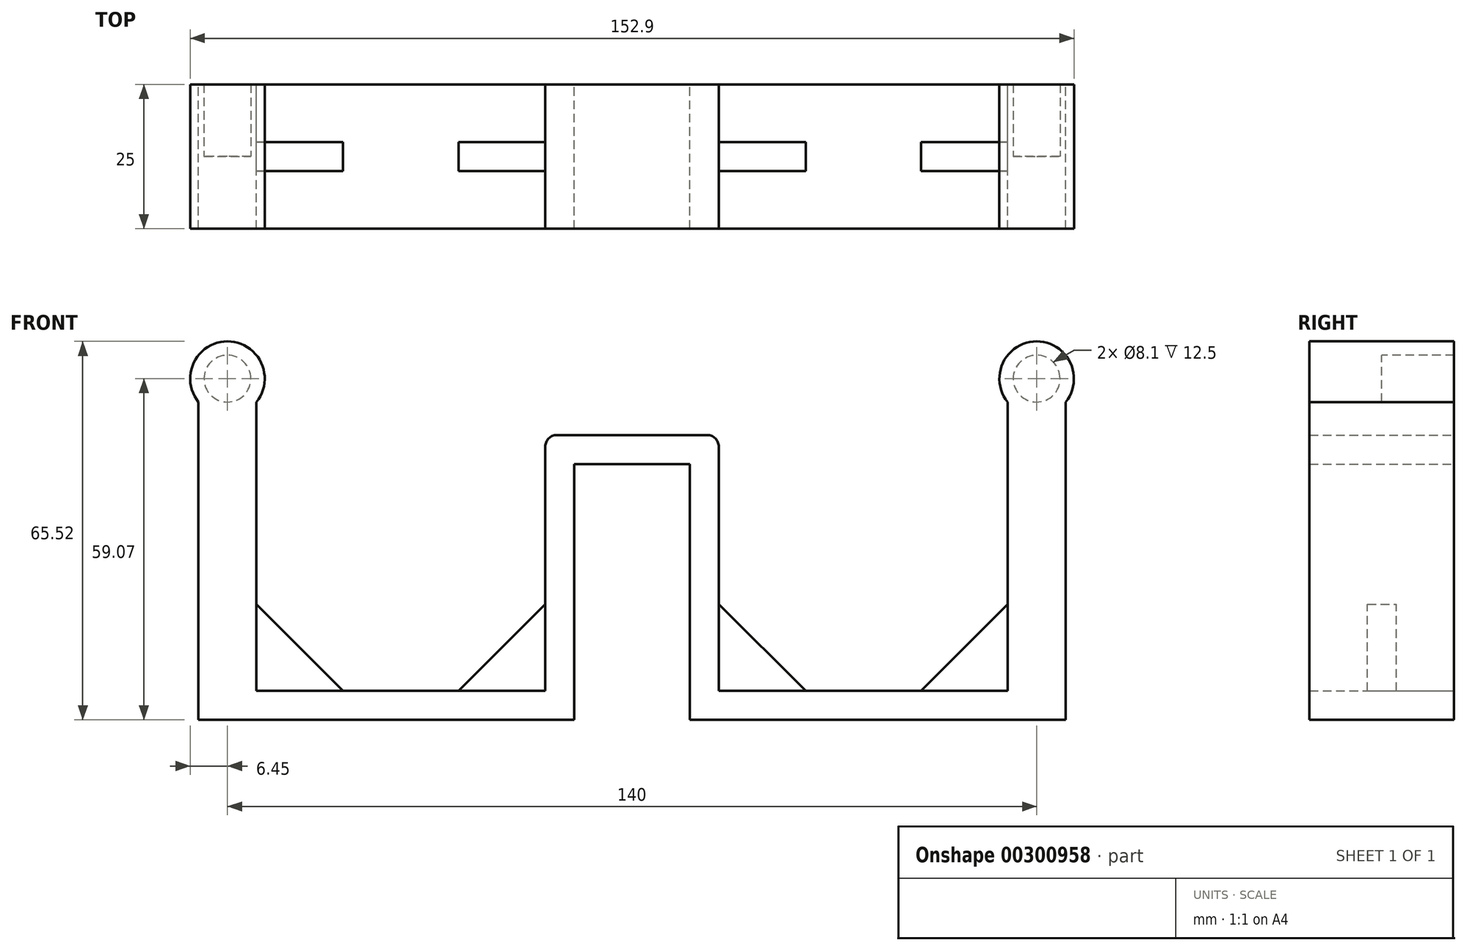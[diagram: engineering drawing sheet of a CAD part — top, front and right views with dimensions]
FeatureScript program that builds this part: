
annotation { "Feature Type Name" : "Feature", "Feature Type Description" : "" }
export const myFeature = defineFeature(function(context is Context, id is Id, definition is map)
    precondition{}
    {
        {
            var Q0;
            Q0=qCreatedBy(makeId("Front.planeOp"),FACE);
            var sketch = newSketch(context, id + "F0", { "sketchPlane" : qUnion([Q0])});
            skLineSegment(sketch, "E0", {"start": v(15, 0) * mm, "end": v(65, 0) * mm});
            skLineSegment(sketch, "E1", {"start": v(65, 0) * mm, "end": v(65, 50) * mm});
            skLineSegment(sketch, "E2", {"start": v(65, 50) * mm, "end": v(75, 50) * mm});
            skLineSegment(sketch, "E3", {"start": v(75, 50) * mm, "end": v(75, -5) * mm});
            skLineSegment(sketch, "E4", {"start": v(75, -5) * mm, "end": v(10, -5) * mm});
            skPoint(sketch, "E5", {"position": v(70, 50) * mm});
            skCircle(sketch, "E6", {"center": v(70, 54.07) * mm, "radius": 6.45 * mm});
            skPoint(sketch, "E7.start.orphan", {"position": v(10, 40) * mm});
            skLineSegment(sketch, "E8", {"start": v(15, 0) * mm, "end": v(15, 44.3) * mm});
            skLineSegment(sketch, "E9", {"start": v(15, 44.3) * mm, "end": v(0, 44.3) * mm});
            skLineSegment(sketch, "E10", {"start": v(0, 44.3) * mm, "end": v(0, 39.3) * mm});
            skLineSegment(sketch, "E11", {"start": v(0, 39.3) * mm, "end": v(10, 39.3) * mm});
            skLineSegment(sketch, "E12", {"start": v(10, 39.3) * mm, "end": v(10, -5) * mm});
            skSolve(sketch);
        }
        {
            var Q0;
            Q0=makeQuery(id+"F0.imprint","IMPRINT",FACE,{"disambiguationData":[TD([[makeQuery(id+"F0.imprint","IMPRINT",EDGE,{"derivedFrom":sQuery(id+"F0.wireOp",EDGE,"E0")}),-1.0]])]});
            var Q1;
            {var subQ0=sQuery(id+"F0.wireOp",EDGE,"E2");Q1=makeQuery(id+"F0.imprint","IMPRINT",FACE,{"disambiguationData":[TD([[makeQuery(id+"F0.imprint","IMPRINT",EDGE,{"derivedFrom":subQ0}),-1.0]])]});}
            var Q2;
            {var subQ0=sQuery(id+"F0.wireOp",EDGE,"E2");Q2=makeQuery(id+"F0.imprint","IMPRINT",FACE,{"disambiguationData":[TD([[makeQuery(id+"F0.imprint","IMPRINT",EDGE,{"derivedFrom":subQ0}),1.0]])]});}
            extrude(context, id + "F1", {"entities" : qUnion([Q0, Q1, Q2]), "endBound" : BoundingType.SYMMETRIC, "depth" : 25 * mm});
        }
        {
            var Q0;
            Q0=qCreatedBy(makeId("Front.planeOp"),FACE);
            var sketch = newSketch(context, id + "F2", { "sketchPlane" : qUnion([Q0])});
            skLineSegment(sketch, "E13", {"start": v(15.04, 0) * mm, "end": v(15.04, 15) * mm});
            skLineSegment(sketch, "E14", {"start": v(15.04, 15) * mm, "end": v(30.04, 0) * mm});
            skLineSegment(sketch, "E15", {"start": v(15.04, 0) * mm, "end": v(30.04, 0) * mm});
            skLineSegment(sketch, "E16", {"start": v(65, 0) * mm, "end": v(65, 15) * mm});
            skLineSegment(sketch, "E17", {"start": v(65, 15) * mm, "end": v(50, 0) * mm});
            skLineSegment(sketch, "E18", {"start": v(50, 0) * mm, "end": v(65, 0) * mm});
            skSolve(sketch);
        }
        {
            var Q0;
            Q0=makeQuery(id+"F2.imprint","IMPRINT",FACE,{"disambiguationData":[TD([[makeQuery(id+"F2.imprint","IMPRINT",EDGE,{"derivedFrom":sQuery(id+"F2.wireOp",EDGE,"E13")}),-1.0]])]});
            var Q1;
            Q1=makeQuery(id+"F2.imprint","IMPRINT",FACE,{"disambiguationData":[TD([[makeQuery(id+"F2.imprint","IMPRINT",EDGE,{"derivedFrom":sQuery(id+"F2.wireOp",EDGE,"E16")}),1.0]])]});
            extrude(context, id + "F3", {"entities" : qUnion([Q0, Q1]), "operationType" : NewBodyOperationType.ADD, "endBound" : BoundingType.SYMMETRIC, "depth" : 5 * mm});
        }
        {
            var Q0;
            Q0=makeQuery(id+"F1.opExtrude","SWEPT_EDGE",EDGE,{"disambiguationData":[OSD([sQuery(id+"F0.wireOp",EDGE,"E8"),sQuery(id+"F0.wireOp",EDGE,"E9")])]});
            var Q1;
            Q1=makeQuery(id+"F7.opPattern","COPY",EDGE,{"derivedFrom":makeQuery(id+"F1.opExtrude","SWEPT_EDGE",EDGE,{"disambiguationData":[OSD([sQuery(id+"F0.wireOp",EDGE,"E8"),sQuery(id+"F0.wireOp",EDGE,"E9")])]}),"instanceName":"1"});
            fillet(context, id + "F4", {"entities" : qUnion([Q0, Q1]), "radius" : 1.98 * mm, "tangentPropagation" : true, "allowEdgeOverflow" : false});
        }
        {
            var Q0;
            Q0=qCreatedBy(makeId("Front.planeOp"),FACE);
            var sketch = newSketch(context, id + "F5", { "sketchPlane" : qUnion([Q0])});
            skCircle(sketch, "E19", {"center": v(70, 54.07) * mm, "radius": 4.05 * mm});
            skSolve(sketch);
        }
        {
            var Q0;
            Q0 = qSketchRegion(id + "F5", true);
            extrude(context, id + "F6", {"entities" : qUnion([Q0]), "operationType" : NewBodyOperationType.REMOVE, "endBound" : BoundingType.UP_TO_NEXT, "oppositeDirection" : true, "depth" : 25 * mm});
        }
        {
            var Q0;
            Q0=makeQuery(id+"F1.opExtrude","SWEPT_BODY",BODY,{"disambiguationData":[OSD([sQuery(id+"F0.wireOp",EDGE,"E0"),sQuery(id+"F0.wireOp",EDGE,"E1"),sQuery(id+"F0.wireOp",EDGE,"E3"),sQuery(id+"F0.wireOp",EDGE,"E4"),sQuery(id+"F0.wireOp",EDGE,"9mlcs2AC-6kd1-qdn8-MNHW-bfPvPwFdCLfu"),sQuery(id+"F0.wireOp",EDGE,"E6"),sQuery(id+"F0.wireOp",EDGE,"E8"),sQuery(id+"F0.wireOp",EDGE,"E9"),sQuery(id+"F0.wireOp",EDGE,"E10"),sQuery(id+"F0.wireOp",EDGE,"E11"),sQuery(id+"F0.wireOp",EDGE,"E12")])]});
            var Q1;
            Q1=qCreatedBy(makeId("Right.planeOp"),FACE);
            mirror(context, id + "F7", {"operationType" : NewBodyOperationType.ADD, "entities" : qUnion([Q0]), "mirrorPlane" : qUnion([Q1])});
        }
    });
